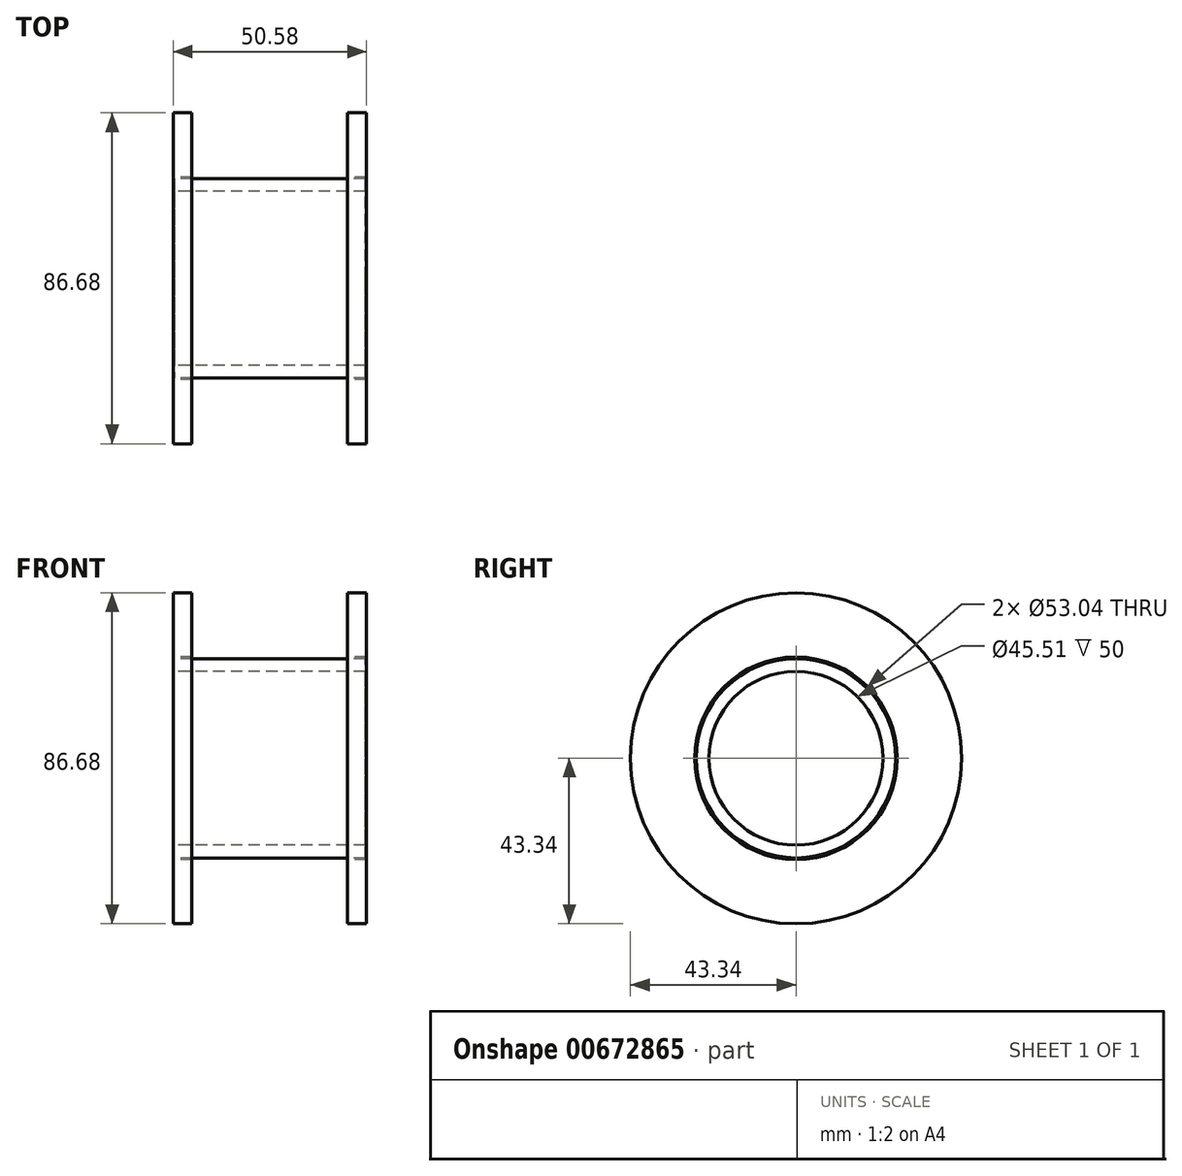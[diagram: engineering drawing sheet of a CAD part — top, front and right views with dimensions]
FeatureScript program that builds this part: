
annotation { "Feature Type Name" : "Feature", "Feature Type Description" : "" }
export const myFeature = defineFeature(function(context is Context, id is Id, definition is map)
    precondition{}
    {
        {
            var Q0;
            Q0=qCreatedBy(makeId("Right.planeOp"),FACE);
            var sketch = newSketch(context, id + "F0", { "sketchPlane" : qUnion([Q0])});
            skCircle(sketch, "E0", {"center": v(0, 0) * mm, "radius": 26.1 * mm});
            skCircle(sketch, "E1", {"center": v(0, 0) * mm, "radius": 22.76 * mm});
            skSolve(sketch);
        }
        {
            var Q0;
            Q0=makeQuery(id+"F0.imprint","IMPRINT",FACE,{"disambiguationData":[TD([[makeQuery(id+"F0.imprint","IMPRINT",EDGE,{"derivedFrom":sQuery(id+"F0.wireOp",EDGE,"E0")}),1.0]])]});
            extrude(context, id + "F1", {"entities" : qUnion([Q0]), "endBound" : BoundingType.SYMMETRIC, "depth" : 50 * mm, "offsetDistance" : 25.4 * mm});
        }
        {
            var Q0;
            Q0=qCreatedBy(makeId("Front.planeOp"),FACE);
            var sketch = newSketch(context, id + "F2", { "sketchPlane" : qUnion([Q0])});
            skLineSegment(sketch, "E2", {"start": v(0, 0) * mm, "end": v(0, 54.56) * mm, "construction": true});
            skLineSegment(sketch, "E3", {"start": v(-25.29, 26.52) * mm, "end": v(25.16, 26.52) * mm, "construction": true});
            skLineSegment(sketch, "E4", {"start": v(-25.29, 26.52) * mm, "end": v(-25.29, 43.34) * mm});
            skLineSegment(sketch, "E5", {"start": v(-25.29, 43.34) * mm, "end": v(-20.37, 43.34) * mm});
            skLineSegment(sketch, "E6", {"start": v(-20.37, 43.34) * mm, "end": v(-20.37, 26.52) * mm});
            skLineSegment(sketch, "E7", {"start": v(-20.37, 26.52) * mm, "end": v(-25.29, 26.52) * mm});
            skLineSegment(sketch, "E8.MirrorCS", {"start": v(25.29, 43.34) * mm, "end": v(20.37, 43.34) * mm});
            skLineSegment(sketch, "E9.MirrorCS", {"start": v(20.37, 43.34) * mm, "end": v(20.37, 26.52) * mm});
            skLineSegment(sketch, "E10.MirrorCS", {"start": v(25.29, 26.52) * mm, "end": v(25.29, 43.34) * mm});
            skLineSegment(sketch, "E11.MirrorCS", {"start": v(20.37, 26.52) * mm, "end": v(25.29, 26.52) * mm});
            skSolve(sketch);
        }
        {
            var Q0;
            Q0=qCreatedBy(makeId("Front.planeOp"),FACE);
            var sketch = newSketch(context, id + "F3", { "sketchPlane" : qUnion([Q0])});
            skLineSegment(sketch, "E12", {"start": v(-25.03, 0) * mm, "end": v(25.16, 0) * mm, "construction": true});
            skSolve(sketch);
        }
        {
            var Q0;
            Q0=makeQuery(id+"F2.imprint","IMPRINT",FACE,{"disambiguationData":[TD([[makeQuery(id+"F2.imprint","IMPRINT",EDGE,{"derivedFrom":sQuery(id+"F2.wireOp",EDGE,"E4")}),-1.0]])]});
            var Q1;
            Q1=makeQuery(id+"F2.imprint","IMPRINT",FACE,{"disambiguationData":[TD([[makeQuery(id+"F2.imprint","IMPRINT",EDGE,{"derivedFrom":sQuery(id+"F2.wireOp",EDGE,"E8.MirrorCS")}),1.0]])]});
            var Q2;
            Q2=sQuery(id+"F3.wireOp",EDGE,"E12");
            revolve(context, id + "F4", {"operationType" : NewBodyOperationType.ADD, "entities" : qUnion([Q0, Q1]), "axis" : qUnion([Q2]), "revolveType" : RevolveType.FULL});
        }
    });
